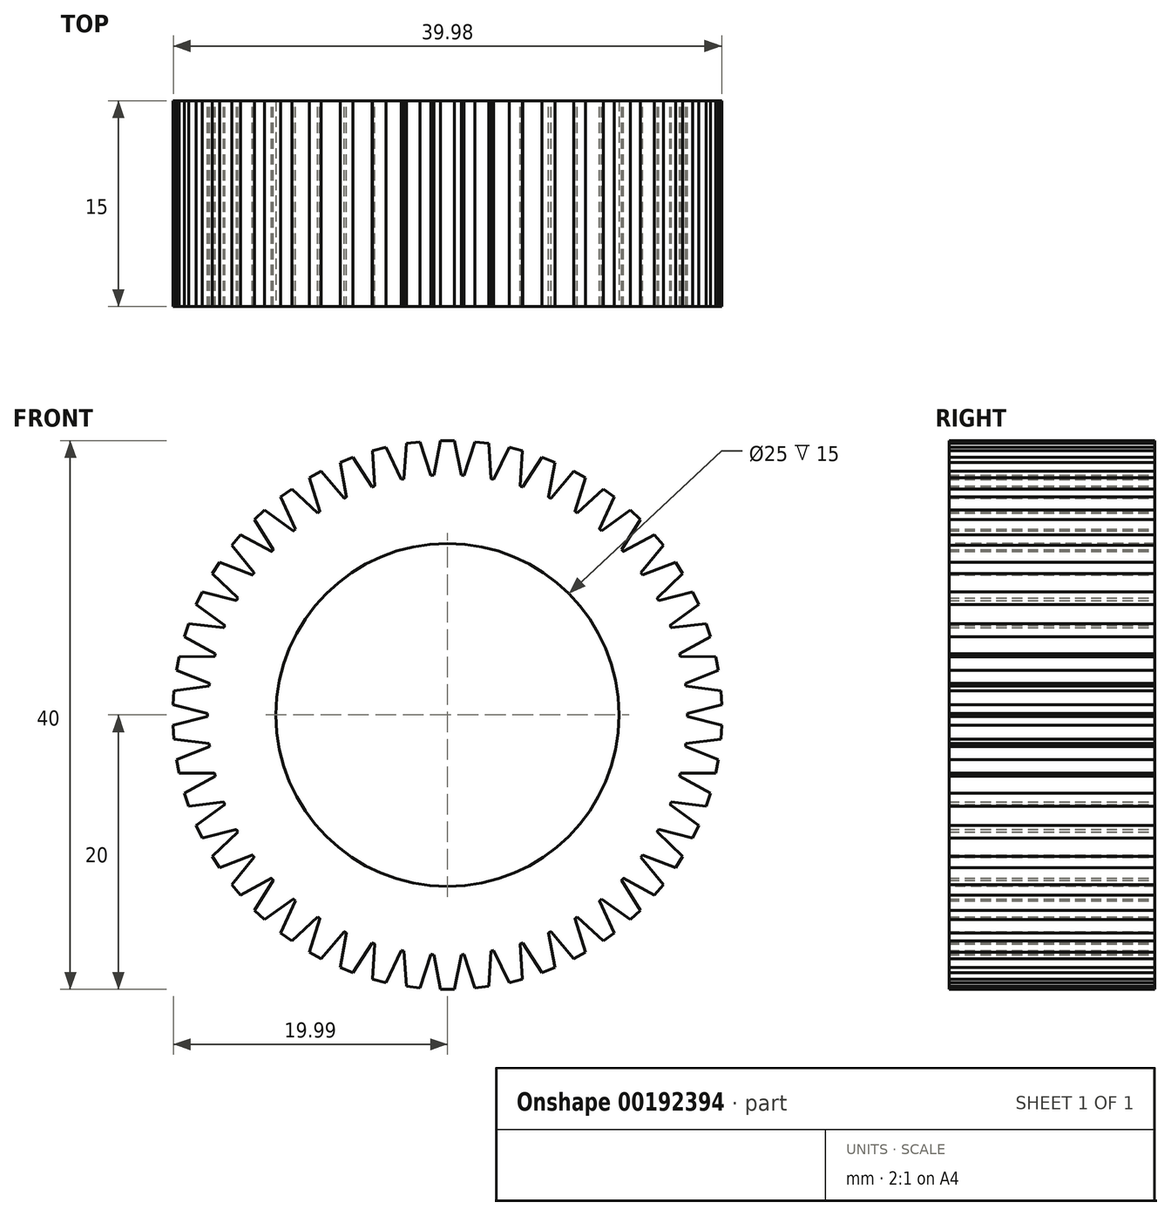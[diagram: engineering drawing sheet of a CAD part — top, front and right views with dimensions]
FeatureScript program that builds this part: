
annotation { "Feature Type Name" : "Feature", "Feature Type Description" : "" }
export const myFeature = defineFeature(function(context is Context, id is Id, definition is map)
    precondition{}
    {
        {
            var Q0;
            Q0=qCreatedBy(makeId("Front.planeOp"),FACE);
            var sketch = newSketch(context, id + "F0", { "sketchPlane" : qUnion([Q0])});
            skCircle(sketch, "E0", {"center": v(0, 0) * mm, "radius": 17.5 * mm});
            skLineSegment(sketch, "E1", {"start": v(-0.5, 20) * mm, "end": v(-1, 17.47) * mm});
            skLineSegment(sketch, "E2.MirrorCS", {"start": v(0.5, 20) * mm, "end": v(1, 17.47) * mm});
            skLineSegment(sketch, "E3", {"start": v(-0.5, 20) * mm, "end": v(0.5, 20) * mm});
            skLineSegment(sketch, "E4.1.0", {"start": v(-3, 19.78) * mm, "end": v(-3.18, 17.2) * mm});
            skLineSegment(sketch, "E4.1.1", {"start": v(-3, 19.78) * mm, "end": v(-2.01, 19.9) * mm});
            skLineSegment(sketch, "E4.1.2", {"start": v(-2.01, 19.9) * mm, "end": v(-1.2, 17.46) * mm});
            skLineSegment(sketch, "E4.2.0", {"start": v(-5.46, 19.25) * mm, "end": v(-5.31, 16.67) * mm});
            skLineSegment(sketch, "E4.2.1", {"start": v(-5.46, 19.25) * mm, "end": v(-4.49, 19.5) * mm});
            skLineSegment(sketch, "E4.2.2", {"start": v(-4.49, 19.5) * mm, "end": v(-3.38, 17.17) * mm});
            skLineSegment(sketch, "E4.3.0", {"start": v(-7.83, 18.41) * mm, "end": v(-7.36, 15.88) * mm});
            skLineSegment(sketch, "E4.3.1", {"start": v(-7.83, 18.41) * mm, "end": v(-6.9, 18.78) * mm});
            skLineSegment(sketch, "E4.3.2", {"start": v(-6.9, 18.78) * mm, "end": v(-5.5, 16.61) * mm});
            skLineSegment(sketch, "E4.4.0", {"start": v(-10.07, 17.29) * mm, "end": v(-9.3, 14.83) * mm});
            skLineSegment(sketch, "E4.4.1", {"start": v(-10.07, 17.29) * mm, "end": v(-9.2, 17.77) * mm});
            skLineSegment(sketch, "E4.4.2", {"start": v(-9.2, 17.77) * mm, "end": v(-7.54, 15.8) * mm});
            skLineSegment(sketch, "E4.5.0", {"start": v(-12.16, 15.89) * mm, "end": v(-11.08, 13.55) * mm});
            skLineSegment(sketch, "E4.5.1", {"start": v(-12.16, 15.89) * mm, "end": v(-11.35, 16.47) * mm});
            skLineSegment(sketch, "E4.5.2", {"start": v(-11.35, 16.47) * mm, "end": v(-9.46, 14.72) * mm});
            skLineSegment(sketch, "E4.6.0", {"start": v(-14.06, 14.24) * mm, "end": v(-12.69, 12.05) * mm});
            skLineSegment(sketch, "E4.6.1", {"start": v(-14.06, 14.24) * mm, "end": v(-13.33, 14.92) * mm});
            skLineSegment(sketch, "E4.6.2", {"start": v(-13.33, 14.92) * mm, "end": v(-11.23, 13.42) * mm});
            skLineSegment(sketch, "E4.7.0", {"start": v(-15.73, 12.36) * mm, "end": v(-14.1, 10.37) * mm});
            skLineSegment(sketch, "E4.7.1", {"start": v(-15.73, 12.36) * mm, "end": v(-15.1, 13.13) * mm});
            skLineSegment(sketch, "E4.7.2", {"start": v(-15.1, 13.13) * mm, "end": v(-12.82, 11.9) * mm});
            skLineSegment(sketch, "E4.8.0", {"start": v(-17.15, 10.3) * mm, "end": v(-15.29, 8.52) * mm});
            skLineSegment(sketch, "E4.8.1", {"start": v(-17.15, 10.3) * mm, "end": v(-16.62, 11.14) * mm});
            skLineSegment(sketch, "E4.8.2", {"start": v(-16.62, 11.14) * mm, "end": v(-14.22, 10.2) * mm});
            skLineSegment(sketch, "E4.9.0", {"start": v(-18.3, 8.06) * mm, "end": v(-16.23, 6.53) * mm});
            skLineSegment(sketch, "E4.9.1", {"start": v(-18.3, 8.06) * mm, "end": v(-17.88, 8.97) * mm});
            skLineSegment(sketch, "E4.9.2", {"start": v(-17.88, 8.97) * mm, "end": v(-15.38, 8.34) * mm});
            skLineSegment(sketch, "E4.10.0", {"start": v(-19.18, 5.7) * mm, "end": v(-16.93, 4.45) * mm});
            skLineSegment(sketch, "E4.10.1", {"start": v(-19.18, 5.7) * mm, "end": v(-18.87, 6.66) * mm});
            skLineSegment(sketch, "E4.10.2", {"start": v(-18.87, 6.66) * mm, "end": v(-16.3, 6.35) * mm});
            skLineSegment(sketch, "E4.11.0", {"start": v(-19.74, 3.26) * mm, "end": v(-17.35, 2.3) * mm});
            skLineSegment(sketch, "E4.11.1", {"start": v(-19.74, 3.26) * mm, "end": v(-19.55, 4.24) * mm});
            skLineSegment(sketch, "E4.11.2", {"start": v(-19.55, 4.24) * mm, "end": v(-16.97, 4.26) * mm});
            skLineSegment(sketch, "E4.12.0", {"start": v(-20, 0.76) * mm, "end": v(-17.5, 0.1) * mm});
            skLineSegment(sketch, "E4.12.1", {"start": v(-20, 0.76) * mm, "end": v(-19.93, 1.75) * mm});
            skLineSegment(sketch, "E4.12.2", {"start": v(-19.93, 1.75) * mm, "end": v(-17.37, 2.1) * mm});
            skLineSegment(sketch, "E4.13.0", {"start": v(-19.93, -1.75) * mm, "end": v(-17.37, -2.1) * mm});
            skLineSegment(sketch, "E4.13.1", {"start": v(-19.93, -1.75) * mm, "end": v(-20, -0.76) * mm});
            skLineSegment(sketch, "E4.13.2", {"start": v(-20, -0.76) * mm, "end": v(-17.5, -0.1) * mm});
            skLineSegment(sketch, "E4.14.0", {"start": v(-19.55, -4.24) * mm, "end": v(-16.97, -4.26) * mm});
            skLineSegment(sketch, "E4.14.1", {"start": v(-19.55, -4.24) * mm, "end": v(-19.74, -3.26) * mm});
            skLineSegment(sketch, "E4.14.2", {"start": v(-19.74, -3.26) * mm, "end": v(-17.35, -2.3) * mm});
            skLineSegment(sketch, "E4.15.0", {"start": v(-18.87, -6.66) * mm, "end": v(-16.3, -6.35) * mm});
            skLineSegment(sketch, "E4.15.1", {"start": v(-18.87, -6.66) * mm, "end": v(-19.18, -5.7) * mm});
            skLineSegment(sketch, "E4.15.2", {"start": v(-19.18, -5.7) * mm, "end": v(-16.93, -4.45) * mm});
            skLineSegment(sketch, "E4.16.0", {"start": v(-17.88, -8.97) * mm, "end": v(-15.38, -8.34) * mm});
            skLineSegment(sketch, "E4.16.1", {"start": v(-17.88, -8.97) * mm, "end": v(-18.3, -8.06) * mm});
            skLineSegment(sketch, "E4.16.2", {"start": v(-18.3, -8.06) * mm, "end": v(-16.23, -6.53) * mm});
            skLineSegment(sketch, "E4.17.0", {"start": v(-16.62, -11.14) * mm, "end": v(-14.22, -10.2) * mm});
            skLineSegment(sketch, "E4.17.1", {"start": v(-16.62, -11.14) * mm, "end": v(-17.15, -10.3) * mm});
            skLineSegment(sketch, "E4.17.2", {"start": v(-17.15, -10.3) * mm, "end": v(-15.29, -8.52) * mm});
            skLineSegment(sketch, "E4.18.0", {"start": v(-15.1, -13.13) * mm, "end": v(-12.82, -11.9) * mm});
            skLineSegment(sketch, "E4.18.1", {"start": v(-15.1, -13.13) * mm, "end": v(-15.73, -12.36) * mm});
            skLineSegment(sketch, "E4.18.2", {"start": v(-15.73, -12.36) * mm, "end": v(-14.1, -10.37) * mm});
            skLineSegment(sketch, "E4.19.0", {"start": v(-13.33, -14.92) * mm, "end": v(-11.23, -13.42) * mm});
            skLineSegment(sketch, "E4.19.1", {"start": v(-13.33, -14.92) * mm, "end": v(-14.06, -14.24) * mm});
            skLineSegment(sketch, "E4.19.2", {"start": v(-14.06, -14.24) * mm, "end": v(-12.69, -12.05) * mm});
            skLineSegment(sketch, "E4.20.0", {"start": v(-11.35, -16.47) * mm, "end": v(-9.46, -14.72) * mm});
            skLineSegment(sketch, "E4.20.1", {"start": v(-11.35, -16.47) * mm, "end": v(-12.16, -15.89) * mm});
            skLineSegment(sketch, "E4.20.2", {"start": v(-12.16, -15.89) * mm, "end": v(-11.08, -13.55) * mm});
            skLineSegment(sketch, "E4.21.0", {"start": v(-9.2, -17.77) * mm, "end": v(-7.54, -15.8) * mm});
            skLineSegment(sketch, "E4.21.1", {"start": v(-9.2, -17.77) * mm, "end": v(-10.07, -17.29) * mm});
            skLineSegment(sketch, "E4.21.2", {"start": v(-10.07, -17.29) * mm, "end": v(-9.3, -14.83) * mm});
            skLineSegment(sketch, "E4.22.0", {"start": v(-6.9, -18.78) * mm, "end": v(-5.5, -16.61) * mm});
            skLineSegment(sketch, "E4.22.1", {"start": v(-6.9, -18.78) * mm, "end": v(-7.83, -18.41) * mm});
            skLineSegment(sketch, "E4.22.2", {"start": v(-7.83, -18.41) * mm, "end": v(-7.36, -15.88) * mm});
            skLineSegment(sketch, "E4.23.0", {"start": v(-4.49, -19.5) * mm, "end": v(-3.38, -17.17) * mm});
            skLineSegment(sketch, "E4.23.1", {"start": v(-4.49, -19.5) * mm, "end": v(-5.46, -19.25) * mm});
            skLineSegment(sketch, "E4.23.2", {"start": v(-5.46, -19.25) * mm, "end": v(-5.31, -16.67) * mm});
            skLineSegment(sketch, "E4.24.0", {"start": v(-2.01, -19.9) * mm, "end": v(-1.2, -17.46) * mm});
            skLineSegment(sketch, "E4.24.1", {"start": v(-2.01, -19.9) * mm, "end": v(-3, -19.78) * mm});
            skLineSegment(sketch, "E4.24.2", {"start": v(-3, -19.78) * mm, "end": v(-3.18, -17.2) * mm});
            skLineSegment(sketch, "E4.25.0", {"start": v(0.5, -20) * mm, "end": v(1, -17.47) * mm});
            skLineSegment(sketch, "E4.25.1", {"start": v(0.5, -20) * mm, "end": v(-0.5, -20) * mm});
            skLineSegment(sketch, "E4.25.2", {"start": v(-0.5, -20) * mm, "end": v(-1, -17.47) * mm});
            skLineSegment(sketch, "E4.26.0", {"start": v(3, -19.78) * mm, "end": v(3.18, -17.2) * mm});
            skLineSegment(sketch, "E4.26.1", {"start": v(3, -19.78) * mm, "end": v(2.01, -19.9) * mm});
            skLineSegment(sketch, "E4.26.2", {"start": v(2.01, -19.9) * mm, "end": v(1.2, -17.46) * mm});
            skLineSegment(sketch, "E4.27.0", {"start": v(5.46, -19.25) * mm, "end": v(5.31, -16.67) * mm});
            skLineSegment(sketch, "E4.27.1", {"start": v(5.46, -19.25) * mm, "end": v(4.49, -19.5) * mm});
            skLineSegment(sketch, "E4.27.2", {"start": v(4.49, -19.5) * mm, "end": v(3.38, -17.17) * mm});
            skLineSegment(sketch, "E4.28.0", {"start": v(7.83, -18.41) * mm, "end": v(7.36, -15.88) * mm});
            skLineSegment(sketch, "E4.28.1", {"start": v(7.83, -18.41) * mm, "end": v(6.9, -18.78) * mm});
            skLineSegment(sketch, "E4.28.2", {"start": v(6.9, -18.78) * mm, "end": v(5.5, -16.61) * mm});
            skLineSegment(sketch, "E4.29.0", {"start": v(10.07, -17.29) * mm, "end": v(9.3, -14.83) * mm});
            skLineSegment(sketch, "E4.29.1", {"start": v(10.07, -17.29) * mm, "end": v(9.2, -17.77) * mm});
            skLineSegment(sketch, "E4.29.2", {"start": v(9.2, -17.77) * mm, "end": v(7.54, -15.8) * mm});
            skLineSegment(sketch, "E4.30.0", {"start": v(12.16, -15.89) * mm, "end": v(11.08, -13.55) * mm});
            skLineSegment(sketch, "E4.30.1", {"start": v(12.16, -15.89) * mm, "end": v(11.35, -16.47) * mm});
            skLineSegment(sketch, "E4.30.2", {"start": v(11.35, -16.47) * mm, "end": v(9.46, -14.72) * mm});
            skLineSegment(sketch, "E4.31.0", {"start": v(14.06, -14.24) * mm, "end": v(12.69, -12.05) * mm});
            skLineSegment(sketch, "E4.31.1", {"start": v(14.06, -14.24) * mm, "end": v(13.33, -14.92) * mm});
            skLineSegment(sketch, "E4.31.2", {"start": v(13.33, -14.92) * mm, "end": v(11.23, -13.42) * mm});
            skLineSegment(sketch, "E4.32.0", {"start": v(15.73, -12.36) * mm, "end": v(14.1, -10.37) * mm});
            skLineSegment(sketch, "E4.32.1", {"start": v(15.73, -12.36) * mm, "end": v(15.1, -13.13) * mm});
            skLineSegment(sketch, "E4.32.2", {"start": v(15.1, -13.13) * mm, "end": v(12.82, -11.9) * mm});
            skLineSegment(sketch, "E4.33.0", {"start": v(17.15, -10.3) * mm, "end": v(15.29, -8.52) * mm});
            skLineSegment(sketch, "E4.33.1", {"start": v(17.15, -10.3) * mm, "end": v(16.62, -11.14) * mm});
            skLineSegment(sketch, "E4.33.2", {"start": v(16.62, -11.14) * mm, "end": v(14.22, -10.2) * mm});
            skLineSegment(sketch, "E4.34.0", {"start": v(18.3, -8.06) * mm, "end": v(16.23, -6.53) * mm});
            skLineSegment(sketch, "E4.34.1", {"start": v(18.3, -8.06) * mm, "end": v(17.88, -8.97) * mm});
            skLineSegment(sketch, "E4.34.2", {"start": v(17.88, -8.97) * mm, "end": v(15.38, -8.34) * mm});
            skLineSegment(sketch, "E4.35.0", {"start": v(19.18, -5.7) * mm, "end": v(16.93, -4.45) * mm});
            skLineSegment(sketch, "E4.35.1", {"start": v(19.18, -5.7) * mm, "end": v(18.87, -6.66) * mm});
            skLineSegment(sketch, "E4.35.2", {"start": v(18.87, -6.66) * mm, "end": v(16.3, -6.35) * mm});
            skLineSegment(sketch, "E4.36.0", {"start": v(19.74, -3.26) * mm, "end": v(17.35, -2.3) * mm});
            skLineSegment(sketch, "E4.36.1", {"start": v(19.74, -3.26) * mm, "end": v(19.55, -4.24) * mm});
            skLineSegment(sketch, "E4.36.2", {"start": v(19.55, -4.24) * mm, "end": v(16.97, -4.26) * mm});
            skLineSegment(sketch, "E4.37.0", {"start": v(20, -0.76) * mm, "end": v(17.5, -0.1) * mm});
            skLineSegment(sketch, "E4.37.1", {"start": v(20, -0.76) * mm, "end": v(19.93, -1.75) * mm});
            skLineSegment(sketch, "E4.37.2", {"start": v(19.93, -1.75) * mm, "end": v(17.37, -2.1) * mm});
            skLineSegment(sketch, "E4.38.0", {"start": v(19.93, 1.75) * mm, "end": v(17.37, 2.1) * mm});
            skLineSegment(sketch, "E4.38.1", {"start": v(19.93, 1.75) * mm, "end": v(20, 0.76) * mm});
            skLineSegment(sketch, "E4.38.2", {"start": v(20, 0.76) * mm, "end": v(17.5, 0.1) * mm});
            skLineSegment(sketch, "E4.39.0", {"start": v(19.55, 4.24) * mm, "end": v(16.97, 4.26) * mm});
            skLineSegment(sketch, "E4.39.1", {"start": v(19.55, 4.24) * mm, "end": v(19.74, 3.26) * mm});
            skLineSegment(sketch, "E4.39.2", {"start": v(19.74, 3.26) * mm, "end": v(17.35, 2.3) * mm});
            skLineSegment(sketch, "E4.40.0", {"start": v(18.87, 6.66) * mm, "end": v(16.3, 6.35) * mm});
            skLineSegment(sketch, "E4.40.1", {"start": v(18.87, 6.66) * mm, "end": v(19.18, 5.7) * mm});
            skLineSegment(sketch, "E4.40.2", {"start": v(19.18, 5.7) * mm, "end": v(16.93, 4.45) * mm});
            skLineSegment(sketch, "E4.41.0", {"start": v(17.88, 8.97) * mm, "end": v(15.38, 8.34) * mm});
            skLineSegment(sketch, "E4.41.1", {"start": v(17.88, 8.97) * mm, "end": v(18.3, 8.06) * mm});
            skLineSegment(sketch, "E4.41.2", {"start": v(18.3, 8.06) * mm, "end": v(16.23, 6.53) * mm});
            skLineSegment(sketch, "E4.42.0", {"start": v(16.62, 11.14) * mm, "end": v(14.22, 10.2) * mm});
            skLineSegment(sketch, "E4.42.1", {"start": v(16.62, 11.14) * mm, "end": v(17.15, 10.3) * mm});
            skLineSegment(sketch, "E4.42.2", {"start": v(17.15, 10.3) * mm, "end": v(15.29, 8.52) * mm});
            skLineSegment(sketch, "E4.43.0", {"start": v(15.1, 13.13) * mm, "end": v(12.82, 11.9) * mm});
            skLineSegment(sketch, "E4.43.1", {"start": v(15.1, 13.13) * mm, "end": v(15.73, 12.36) * mm});
            skLineSegment(sketch, "E4.43.2", {"start": v(15.73, 12.36) * mm, "end": v(14.1, 10.37) * mm});
            skLineSegment(sketch, "E4.44.0", {"start": v(13.33, 14.92) * mm, "end": v(11.23, 13.42) * mm});
            skLineSegment(sketch, "E4.44.1", {"start": v(13.33, 14.92) * mm, "end": v(14.06, 14.24) * mm});
            skLineSegment(sketch, "E4.44.2", {"start": v(14.06, 14.24) * mm, "end": v(12.69, 12.05) * mm});
            skLineSegment(sketch, "E4.45.0", {"start": v(11.35, 16.47) * mm, "end": v(9.46, 14.72) * mm});
            skLineSegment(sketch, "E4.45.1", {"start": v(11.35, 16.47) * mm, "end": v(12.16, 15.89) * mm});
            skLineSegment(sketch, "E4.45.2", {"start": v(12.16, 15.89) * mm, "end": v(11.08, 13.55) * mm});
            skLineSegment(sketch, "E4.46.0", {"start": v(9.2, 17.77) * mm, "end": v(7.54, 15.8) * mm});
            skLineSegment(sketch, "E4.46.1", {"start": v(9.2, 17.77) * mm, "end": v(10.07, 17.29) * mm});
            skLineSegment(sketch, "E4.46.2", {"start": v(10.07, 17.29) * mm, "end": v(9.3, 14.83) * mm});
            skLineSegment(sketch, "E4.47.0", {"start": v(6.9, 18.78) * mm, "end": v(5.5, 16.61) * mm});
            skLineSegment(sketch, "E4.47.1", {"start": v(6.9, 18.78) * mm, "end": v(7.83, 18.41) * mm});
            skLineSegment(sketch, "E4.47.2", {"start": v(7.83, 18.41) * mm, "end": v(7.36, 15.88) * mm});
            skLineSegment(sketch, "E4.48.0", {"start": v(4.49, 19.5) * mm, "end": v(3.38, 17.17) * mm});
            skLineSegment(sketch, "E4.48.1", {"start": v(4.49, 19.5) * mm, "end": v(5.46, 19.25) * mm});
            skLineSegment(sketch, "E4.48.2", {"start": v(5.46, 19.25) * mm, "end": v(5.31, 16.67) * mm});
            skLineSegment(sketch, "E4.49.0", {"start": v(2.01, 19.9) * mm, "end": v(1.2, 17.46) * mm});
            skLineSegment(sketch, "E4.49.1", {"start": v(2.01, 19.9) * mm, "end": v(3, 19.78) * mm});
            skLineSegment(sketch, "E4.49.2", {"start": v(3, 19.78) * mm, "end": v(3.18, 17.2) * mm});
            skSolve(sketch);
        }
        {
            var Q0;
            Q0 = qSketchRegion(id + "F0", true);
            extrude(context, id + "F1", {"entities" : qUnion([Q0]), "depth" : 15 * mm});
        }
        {
            var Q0;
            Q0=makeQuery(id+"F1.opExtrude","CAP_FACE",FACE,{"disambiguationData":[OSD([sQuery(id+"F0.wireOp",EDGE,"E0"),sQuery(id+"F0.wireOp",EDGE,"E1"),sQuery(id+"F0.wireOp",EDGE,"E2.MirrorCS"),sQuery(id+"F0.wireOp",EDGE,"E3"),sQuery(id+"F0.wireOp",EDGE,"E4.1.0"),sQuery(id+"F0.wireOp",EDGE,"E4.1.1"),sQuery(id+"F0.wireOp",EDGE,"E4.1.2"),sQuery(id+"F0.wireOp",EDGE,"E4.2.0"),sQuery(id+"F0.wireOp",EDGE,"E4.2.1"),sQuery(id+"F0.wireOp",EDGE,"E4.2.2"),sQuery(id+"F0.wireOp",EDGE,"E4.3.0"),sQuery(id+"F0.wireOp",EDGE,"E4.3.1"),sQuery(id+"F0.wireOp",EDGE,"E4.3.2"),sQuery(id+"F0.wireOp",EDGE,"E4.4.0"),sQuery(id+"F0.wireOp",EDGE,"E4.4.1"),sQuery(id+"F0.wireOp",EDGE,"E4.4.2"),sQuery(id+"F0.wireOp",EDGE,"E4.5.0"),sQuery(id+"F0.wireOp",EDGE,"E4.5.1"),sQuery(id+"F0.wireOp",EDGE,"E4.5.2"),sQuery(id+"F0.wireOp",EDGE,"E4.6.0"),sQuery(id+"F0.wireOp",EDGE,"E4.6.1"),sQuery(id+"F0.wireOp",EDGE,"E4.6.2"),sQuery(id+"F0.wireOp",EDGE,"E4.7.0"),sQuery(id+"F0.wireOp",EDGE,"E4.7.1"),sQuery(id+"F0.wireOp",EDGE,"E4.7.2"),sQuery(id+"F0.wireOp",EDGE,"E4.8.0"),sQuery(id+"F0.wireOp",EDGE,"E4.8.1"),sQuery(id+"F0.wireOp",EDGE,"E4.8.2"),sQuery(id+"F0.wireOp",EDGE,"E4.9.0"),sQuery(id+"F0.wireOp",EDGE,"E4.9.1"),sQuery(id+"F0.wireOp",EDGE,"E4.9.2"),sQuery(id+"F0.wireOp",EDGE,"E4.10.0"),sQuery(id+"F0.wireOp",EDGE,"E4.10.1"),sQuery(id+"F0.wireOp",EDGE,"E4.10.2"),sQuery(id+"F0.wireOp",EDGE,"E4.11.0"),sQuery(id+"F0.wireOp",EDGE,"E4.11.1"),sQuery(id+"F0.wireOp",EDGE,"E4.11.2"),sQuery(id+"F0.wireOp",EDGE,"E4.12.0"),sQuery(id+"F0.wireOp",EDGE,"E4.12.1"),sQuery(id+"F0.wireOp",EDGE,"E4.12.2"),sQuery(id+"F0.wireOp",EDGE,"E4.13.0"),sQuery(id+"F0.wireOp",EDGE,"E4.13.1"),sQuery(id+"F0.wireOp",EDGE,"E4.13.2"),sQuery(id+"F0.wireOp",EDGE,"E4.14.0"),sQuery(id+"F0.wireOp",EDGE,"E4.14.1"),sQuery(id+"F0.wireOp",EDGE,"E4.14.2"),sQuery(id+"F0.wireOp",EDGE,"E4.15.0"),sQuery(id+"F0.wireOp",EDGE,"E4.15.1"),sQuery(id+"F0.wireOp",EDGE,"E4.15.2"),sQuery(id+"F0.wireOp",EDGE,"E4.16.0"),sQuery(id+"F0.wireOp",EDGE,"E4.16.1"),sQuery(id+"F0.wireOp",EDGE,"E4.16.2"),sQuery(id+"F0.wireOp",EDGE,"E4.17.0"),sQuery(id+"F0.wireOp",EDGE,"E4.17.1"),sQuery(id+"F0.wireOp",EDGE,"E4.17.2"),sQuery(id+"F0.wireOp",EDGE,"E4.18.0"),sQuery(id+"F0.wireOp",EDGE,"E4.18.1"),sQuery(id+"F0.wireOp",EDGE,"E4.18.2"),sQuery(id+"F0.wireOp",EDGE,"E4.19.0"),sQuery(id+"F0.wireOp",EDGE,"E4.19.1"),sQuery(id+"F0.wireOp",EDGE,"E4.19.2"),sQuery(id+"F0.wireOp",EDGE,"E4.20.0"),sQuery(id+"F0.wireOp",EDGE,"E4.20.1"),sQuery(id+"F0.wireOp",EDGE,"E4.20.2"),sQuery(id+"F0.wireOp",EDGE,"E4.21.0"),sQuery(id+"F0.wireOp",EDGE,"E4.21.1"),sQuery(id+"F0.wireOp",EDGE,"E4.21.2"),sQuery(id+"F0.wireOp",EDGE,"E4.22.0"),sQuery(id+"F0.wireOp",EDGE,"E4.22.1"),sQuery(id+"F0.wireOp",EDGE,"E4.22.2"),sQuery(id+"F0.wireOp",EDGE,"E4.23.0"),sQuery(id+"F0.wireOp",EDGE,"E4.23.1"),sQuery(id+"F0.wireOp",EDGE,"E4.23.2"),sQuery(id+"F0.wireOp",EDGE,"E4.24.0"),sQuery(id+"F0.wireOp",EDGE,"E4.24.1"),sQuery(id+"F0.wireOp",EDGE,"E4.24.2"),sQuery(id+"F0.wireOp",EDGE,"E4.25.0"),sQuery(id+"F0.wireOp",EDGE,"E4.25.1"),sQuery(id+"F0.wireOp",EDGE,"E4.25.2"),sQuery(id+"F0.wireOp",EDGE,"E4.26.0"),sQuery(id+"F0.wireOp",EDGE,"E4.26.1"),sQuery(id+"F0.wireOp",EDGE,"E4.26.2"),sQuery(id+"F0.wireOp",EDGE,"E4.27.0"),sQuery(id+"F0.wireOp",EDGE,"E4.27.1"),sQuery(id+"F0.wireOp",EDGE,"E4.27.2"),sQuery(id+"F0.wireOp",EDGE,"E4.28.0"),sQuery(id+"F0.wireOp",EDGE,"E4.28.1"),sQuery(id+"F0.wireOp",EDGE,"E4.28.2"),sQuery(id+"F0.wireOp",EDGE,"E4.29.0"),sQuery(id+"F0.wireOp",EDGE,"E4.29.1"),sQuery(id+"F0.wireOp",EDGE,"E4.29.2"),sQuery(id+"F0.wireOp",EDGE,"E4.30.0"),sQuery(id+"F0.wireOp",EDGE,"E4.30.1"),sQuery(id+"F0.wireOp",EDGE,"E4.30.2"),sQuery(id+"F0.wireOp",EDGE,"E4.31.0"),sQuery(id+"F0.wireOp",EDGE,"E4.31.1"),sQuery(id+"F0.wireOp",EDGE,"E4.31.2"),sQuery(id+"F0.wireOp",EDGE,"E4.32.0"),sQuery(id+"F0.wireOp",EDGE,"E4.32.1"),sQuery(id+"F0.wireOp",EDGE,"E4.32.2"),sQuery(id+"F0.wireOp",EDGE,"E4.33.0"),sQuery(id+"F0.wireOp",EDGE,"E4.33.1"),sQuery(id+"F0.wireOp",EDGE,"E4.33.2"),sQuery(id+"F0.wireOp",EDGE,"E4.34.0"),sQuery(id+"F0.wireOp",EDGE,"E4.34.1"),sQuery(id+"F0.wireOp",EDGE,"E4.34.2"),sQuery(id+"F0.wireOp",EDGE,"E4.35.0"),sQuery(id+"F0.wireOp",EDGE,"E4.35.1"),sQuery(id+"F0.wireOp",EDGE,"E4.35.2"),sQuery(id+"F0.wireOp",EDGE,"E4.36.0"),sQuery(id+"F0.wireOp",EDGE,"E4.36.1"),sQuery(id+"F0.wireOp",EDGE,"E4.36.2"),sQuery(id+"F0.wireOp",EDGE,"E4.37.0"),sQuery(id+"F0.wireOp",EDGE,"E4.37.1"),sQuery(id+"F0.wireOp",EDGE,"E4.37.2"),sQuery(id+"F0.wireOp",EDGE,"E4.38.0"),sQuery(id+"F0.wireOp",EDGE,"E4.38.1"),sQuery(id+"F0.wireOp",EDGE,"E4.38.2"),sQuery(id+"F0.wireOp",EDGE,"E4.39.0"),sQuery(id+"F0.wireOp",EDGE,"E4.39.1"),sQuery(id+"F0.wireOp",EDGE,"E4.39.2"),sQuery(id+"F0.wireOp",EDGE,"E4.40.0"),sQuery(id+"F0.wireOp",EDGE,"E4.40.1"),sQuery(id+"F0.wireOp",EDGE,"E4.40.2"),sQuery(id+"F0.wireOp",EDGE,"E4.41.0"),sQuery(id+"F0.wireOp",EDGE,"E4.41.1"),sQuery(id+"F0.wireOp",EDGE,"E4.41.2"),sQuery(id+"F0.wireOp",EDGE,"E4.42.0"),sQuery(id+"F0.wireOp",EDGE,"E4.42.1"),sQuery(id+"F0.wireOp",EDGE,"E4.42.2"),sQuery(id+"F0.wireOp",EDGE,"E4.43.0"),sQuery(id+"F0.wireOp",EDGE,"E4.43.1"),sQuery(id+"F0.wireOp",EDGE,"E4.43.2"),sQuery(id+"F0.wireOp",EDGE,"E4.44.0"),sQuery(id+"F0.wireOp",EDGE,"E4.44.1"),sQuery(id+"F0.wireOp",EDGE,"E4.44.2"),sQuery(id+"F0.wireOp",EDGE,"E4.45.0"),sQuery(id+"F0.wireOp",EDGE,"E4.45.1"),sQuery(id+"F0.wireOp",EDGE,"E4.45.2"),sQuery(id+"F0.wireOp",EDGE,"E4.46.0"),sQuery(id+"F0.wireOp",EDGE,"E4.46.1"),sQuery(id+"F0.wireOp",EDGE,"E4.46.2"),sQuery(id+"F0.wireOp",EDGE,"E4.47.0"),sQuery(id+"F0.wireOp",EDGE,"E4.47.1"),sQuery(id+"F0.wireOp",EDGE,"E4.47.2"),sQuery(id+"F0.wireOp",EDGE,"E4.48.0"),sQuery(id+"F0.wireOp",EDGE,"E4.48.1"),sQuery(id+"F0.wireOp",EDGE,"E4.48.2"),sQuery(id+"F0.wireOp",EDGE,"E4.49.0"),sQuery(id+"F0.wireOp",EDGE,"E4.49.1"),sQuery(id+"F0.wireOp",EDGE,"E4.49.2")])],"isStart":false});
            var sketch = newSketch(context, id + "F2", { "sketchPlane" : qUnion([Q0])});
            skCircle(sketch, "E5", {"center": v(0, 0) * mm, "radius": 12.5 * mm});
            skSolve(sketch);
        }
        {
            var Q0;
            Q0=makeQuery(id+"F2.imprint","IMPRINT",FACE,{"disambiguationData":[TD([[makeQuery(id+"F2.imprint","IMPRINT",EDGE,{"derivedFrom":sQuery(id+"F2.wireOp",EDGE,"E5")}),1.0]])]});
            var Q1;
            Q1=sQuery(id+"F2.wireOp",EDGE,"E5");
            extrude(context, id + "F3", {"entities" : qUnion([Q0]), "operationType" : NewBodyOperationType.REMOVE, "surfaceEntities" : qUnion([Q1]), "endBound" : BoundingType.THROUGH_ALL, "oppositeDirection" : true, "depth" : 25 * mm});
        }
    });
